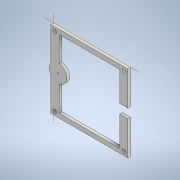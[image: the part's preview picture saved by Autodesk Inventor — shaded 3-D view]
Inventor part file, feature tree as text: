
AUTODESK INVENTOR PART (.ipt)
format: ipt  version: 2022 (Build 260153000, 153)  size: 126,464 bytes
history: native  units: mm
features: other x1, extrude x1, sketch x1
ambient origin geometry x8: Origin, YZ Plane, XZ Plane, XY Plane, X Axis, Y Axis, Z Axis, Center Point
bodies: Body1 (feature_tree)
feature tree (3):
  other  "Sólido1"
  extrude  "Extrusión1"  Depth=5.0mm TaperAngle=0.0deg
  sketch  "Boceto1"  dims[d0=2.0mm d1=5.0mm d2=0.0mm]
